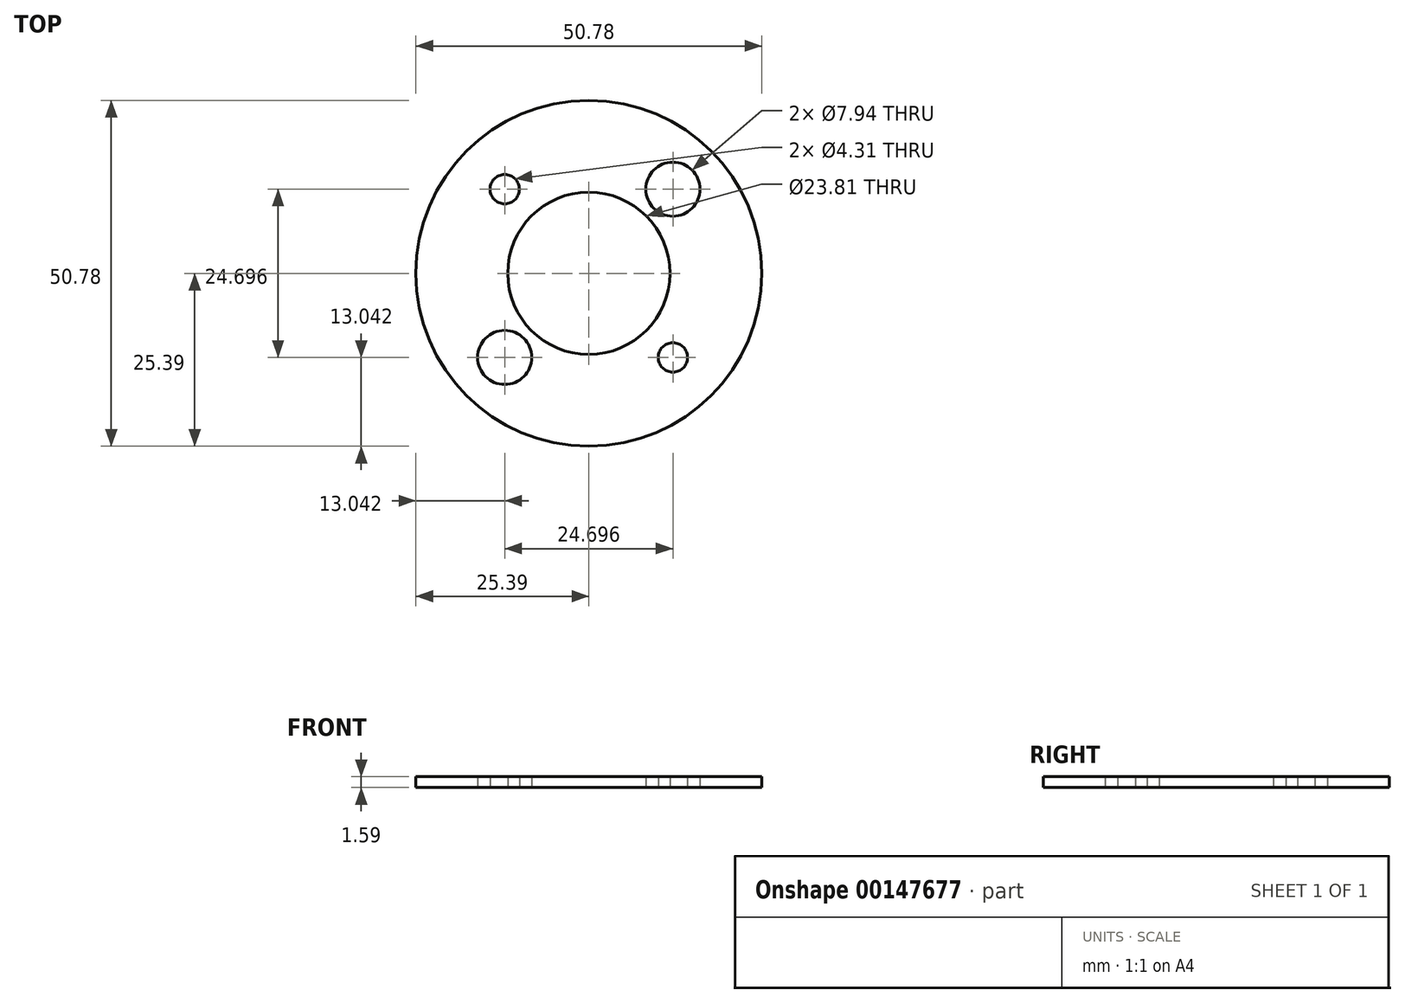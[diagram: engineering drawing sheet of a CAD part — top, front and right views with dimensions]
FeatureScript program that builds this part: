
annotation { "Feature Type Name" : "Feature", "Feature Type Description" : "" }
export const myFeature = defineFeature(function(context is Context, id is Id, definition is map)
    precondition{}
    {
        {
            var Q0;
            Q0=qCreatedBy(makeId("Top.planeOp"),FACE);
            var sketch = newSketch(context, id + "F0", { "sketchPlane" : qUnion([Q0])});
            skCircle(sketch, "E0", {"center": v(0, 0) * mm, "radius": 25.4 * mm});
            skCircle(sketch, "E1", {"center": v(0, 0) * mm, "radius": 11.9 * mm});
            skLineSegment(sketch, "E2.bottom", {"start": v(-12.35, 12.35) * mm, "end": v(12.35, 12.35) * mm, "construction": true});
            skLineSegment(sketch, "E2.top", {"start": v(-12.35, -12.35) * mm, "end": v(12.35, -12.35) * mm, "construction": true});
            skLineSegment(sketch, "E2.left", {"start": v(-12.35, 12.35) * mm, "end": v(-12.35, -12.35) * mm, "construction": true});
            skLineSegment(sketch, "E2.right", {"start": v(12.35, 12.35) * mm, "end": v(12.35, -12.35) * mm, "construction": true});
            skCircle(sketch, "E3", {"center": v(-12.35, 12.35) * mm, "radius": 5.56 * mm, "construction": true});
            skCircle(sketch, "E4", {"center": v(12.35, 12.35) * mm, "radius": 3.97 * mm});
            skCircle(sketch, "E5", {"center": v(-12.35, 12.35) * mm, "radius": 2.15 * mm});
            skCircle(sketch, "E6", {"center": v(-12.35, -12.35) * mm, "radius": 3.97 * mm});
            skCircle(sketch, "E7", {"center": v(12.35, -12.35) * mm, "radius": 2.15 * mm});
            skSolve(sketch);
        }
        {
            var Q0;
            Q0=qSketchRegion(id+"F0",true);
            extrude(context, id + "F1", {"entities" : qUnion([Q0]), "depth" : 1.59 * mm});
        }
    });
